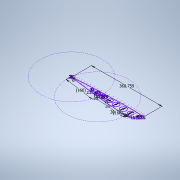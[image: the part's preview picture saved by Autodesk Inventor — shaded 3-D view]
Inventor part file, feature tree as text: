
AUTODESK INVENTOR PART (.ipt)
format: ipt  version: 2022 (Build 260153000, 153)  size: 155,648 bytes
history: native  units: mm
features: sketch x1
ambient origin geometry x8: Origin, YZ Plane, XZ Plane, XY Plane, X Axis, Y Axis, Z Axis, Center Point
feature tree (1):
  sketch  "Sketch1"  dims[d5=160.0mm d8=160.0mm d17=5.0mm d18=5.0mm d25=6.0mm d26=5.0mm d27=5.0mm d30=17.227785mm d31=34.456mm d36=5.0mm d37=5.0mm d41=23.0mm d50=368.759386mm d51=15.0mm d52=28.0mm d53=30.0mm d54=25.0mm d57=15.0mm d58=15.0mm d59=25.0mm d60=8.0mm d61=23.0mm d62=20.0mm]
